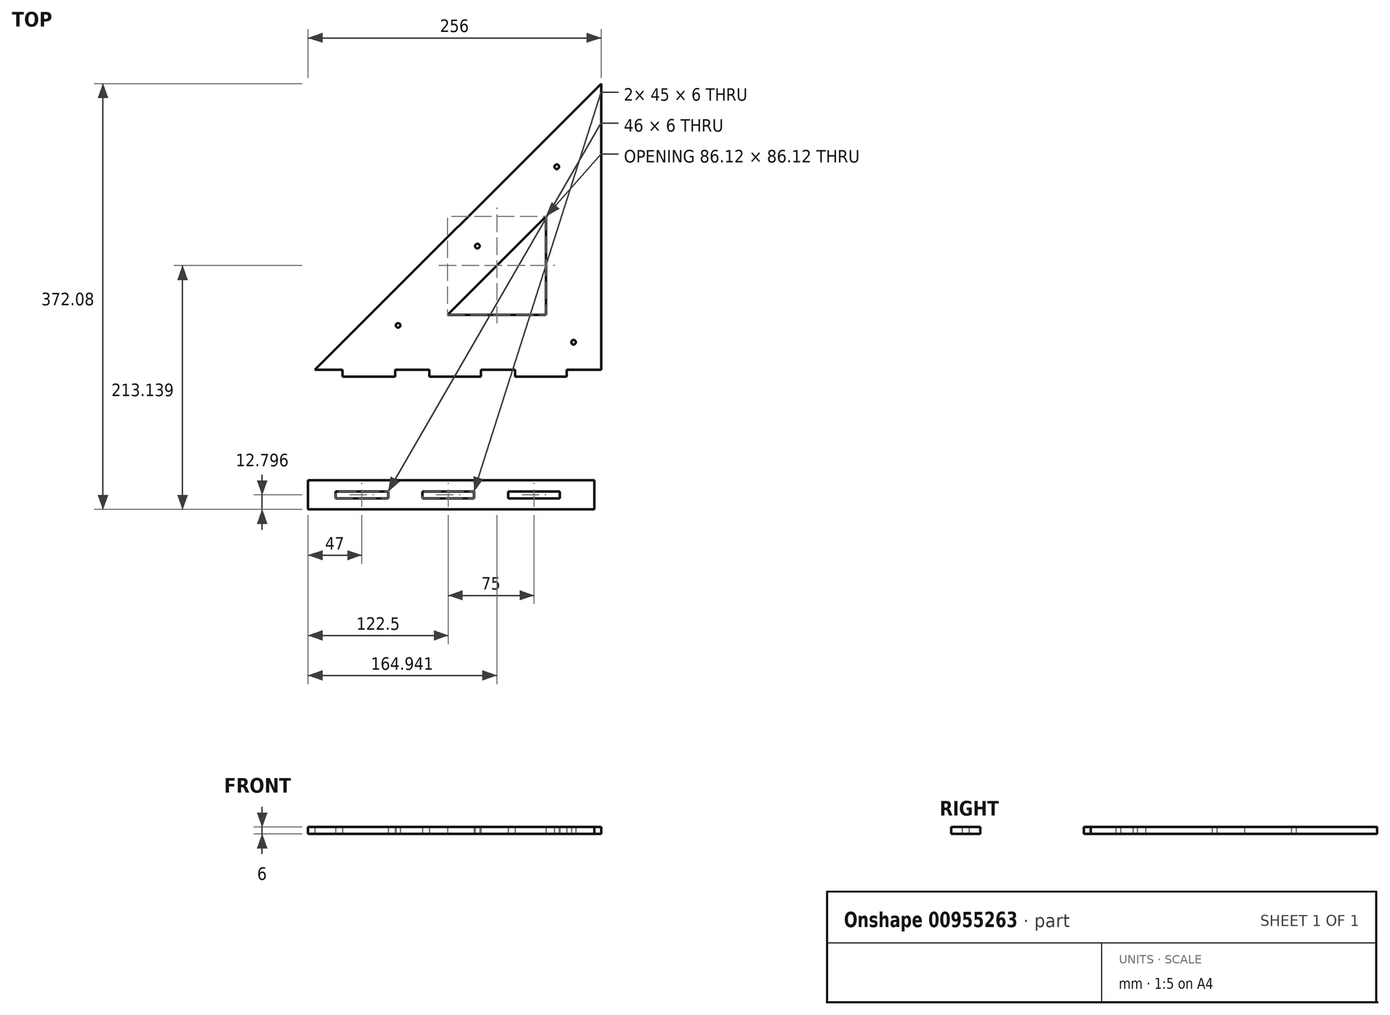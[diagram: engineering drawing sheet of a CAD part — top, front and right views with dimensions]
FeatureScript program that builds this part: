
annotation { "Feature Type Name" : "Feature", "Feature Type Description" : "" }
export const myFeature = defineFeature(function(context is Context, id is Id, definition is map)
    precondition{}
    {
        {
            var Q0;
            Q0=qCreatedBy(makeId("Top.planeOp"),FACE);
            var sketch = newSketch(context, id + "F0", { "sketchPlane" : qUnion([Q0])});
            skLineSegment(sketch, "E0", {"start": v(30, 0) * mm, "end": v(76, 0) * mm});
            skLineSegment(sketch, "E1", {"start": v(256, 6) * mm, "end": v(256, 256) * mm});
            skLineSegment(sketch, "E2", {"start": v(256, 256) * mm, "end": v(6, 6) * mm});
            skLineSegment(sketch, "E3.0", {"start": v(208, 140.12) * mm, "end": v(121.88, 54) * mm});
            skLineSegment(sketch, "E3.1", {"start": v(208, 54) * mm, "end": v(208, 140.12) * mm});
            skLineSegment(sketch, "E3.2", {"start": v(121.88, 54) * mm, "end": v(208, 54) * mm});
            skCircle(sketch, "E4", {"center": v(147.97, 114.03) * mm, "radius": 2 * mm});
            skCircle(sketch, "E5", {"center": v(78.67, 44.73) * mm, "radius": 2 * mm});
            skCircle(sketch, "E6", {"center": v(217.27, 183.33) * mm, "radius": 2 * mm});
            skLineSegment(sketch, "E7.top", {"start": v(6, 6) * mm, "end": v(30, 6) * mm});
            skLineSegment(sketch, "E7.right", {"start": v(30, 0) * mm, "end": v(30, 6) * mm});
            skLineSegment(sketch, "E8.top", {"start": v(76, 6) * mm, "end": v(106, 6) * mm});
            skLineSegment(sketch, "E8.left", {"start": v(76, 0) * mm, "end": v(76, 6) * mm});
            skLineSegment(sketch, "E8.right", {"start": v(106, 0) * mm, "end": v(106, 6) * mm});
            skLineSegment(sketch, "E9.top", {"start": v(226, 6) * mm, "end": v(256, 6) * mm});
            skLineSegment(sketch, "E9.left", {"start": v(226, 0) * mm, "end": v(226, 6) * mm});
            skLineSegment(sketch, "E10.top", {"start": v(151, 6) * mm, "end": v(181, 6) * mm});
            skLineSegment(sketch, "E10.left", {"start": v(151, 0) * mm, "end": v(151, 6) * mm});
            skLineSegment(sketch, "E10.right", {"start": v(181, 0) * mm, "end": v(181, 6) * mm});
            skLineSegment(sketch, "E11.bottom", {"start": v(0, -90.48) * mm, "end": v(250, -90.48) * mm});
            skLineSegment(sketch, "E11.top", {"start": v(0, -116.08) * mm, "end": v(250, -116.08) * mm});
            skLineSegment(sketch, "E11.left", {"start": v(0, -90.48) * mm, "end": v(0, -116.08) * mm});
            skLineSegment(sketch, "E11.right", {"start": v(250, -90.48) * mm, "end": v(250, -116.08) * mm});
            skLineSegment(sketch, "E12", {"start": v(0, -103.28) * mm, "end": v(250, -103.28) * mm, "construction": true});
            skLineSegment(sketch, "E13.bottom", {"start": v(175, -106.28) * mm, "end": v(220, -106.28) * mm});
            skLineSegment(sketch, "E13.top", {"start": v(175, -100.28) * mm, "end": v(220, -100.28) * mm});
            skLineSegment(sketch, "E13.left", {"start": v(175, -106.28) * mm, "end": v(175, -100.28) * mm});
            skLineSegment(sketch, "E13.right", {"start": v(220, -106.28) * mm, "end": v(220, -100.28) * mm});
            skPoint(sketch, "E13.middle", {"position": v(197.5, -103.28) * mm});
            skLineSegment(sketch, "E14.bottom", {"start": v(24, -106.28) * mm, "end": v(70, -106.28) * mm});
            skLineSegment(sketch, "E14.top", {"start": v(24, -100.28) * mm, "end": v(70, -100.28) * mm});
            skLineSegment(sketch, "E14.left", {"start": v(24, -106.28) * mm, "end": v(24, -100.28) * mm});
            skLineSegment(sketch, "E14.right", {"start": v(70, -106.28) * mm, "end": v(70, -100.28) * mm});
            skPoint(sketch, "E14.middle", {"position": v(47, -103.28) * mm});
            skLineSegment(sketch, "E15.bottom", {"start": v(145, -106.28) * mm, "end": v(100, -106.28) * mm});
            skLineSegment(sketch, "E15.top", {"start": v(145, -100.28) * mm, "end": v(100, -100.28) * mm});
            skLineSegment(sketch, "E15.left", {"start": v(145, -106.28) * mm, "end": v(145, -100.28) * mm});
            skLineSegment(sketch, "E15.right", {"start": v(100, -106.28) * mm, "end": v(100, -100.28) * mm});
            skPoint(sketch, "E15.middle", {"position": v(122.5, -103.28) * mm});
            skLineSegment(sketch, "E16.trimOffspring", {"start": v(106, 0) * mm, "end": v(151, 0) * mm});
            skLineSegment(sketch, "E17.trimOffspring", {"start": v(181, 0) * mm, "end": v(226, 0) * mm});
            skLineSegment(sketch, "E18", {"start": v(30, 6) * mm, "end": v(76, 6) * mm, "construction": true});
            skPoint(sketch, "E19.orphan", {"position": v(34.65, 0) * mm});
            skLineSegment(sketch, "E20", {"start": v(256, 222.06) * mm, "end": v(39.94, 6) * mm, "construction": true});
            skLineSegment(sketch, "E21", {"start": v(147.97, 114.03) * mm, "end": v(256, 6) * mm, "construction": true});
            skCircle(sketch, "E22", {"center": v(232, 30) * mm, "radius": 2 * mm});
            skSolve(sketch);
        }
        {
            var Q0;
            Q0=makeQuery(id+"F0.imprint","IMPRINT",FACE,{"disambiguationData":[TD([[makeQuery(id+"F0.imprint","IMPRINT",EDGE,{"derivedFrom":sQuery(id+"F0.wireOp",EDGE,"E0")}),1.0]])]});
            extrude(context, id + "F1", {"entities" : qUnion([Q0]), "depth" : 6 * mm, "offsetDistance" : 25 * mm});
        }
        {
            var Q0;
            Q0=makeQuery(id+"F0.imprint","IMPRINT",FACE,{"disambiguationData":[TD([[makeQuery(id+"F0.imprint","IMPRINT",EDGE,{"derivedFrom":sQuery(id+"F0.wireOp",EDGE,"E11.bottom")}),-1.0]])]});
            extrude(context, id + "F2", {"entities" : qUnion([Q0]), "depth" : 6 * mm, "offsetDistance" : 25 * mm});
        }
    });
